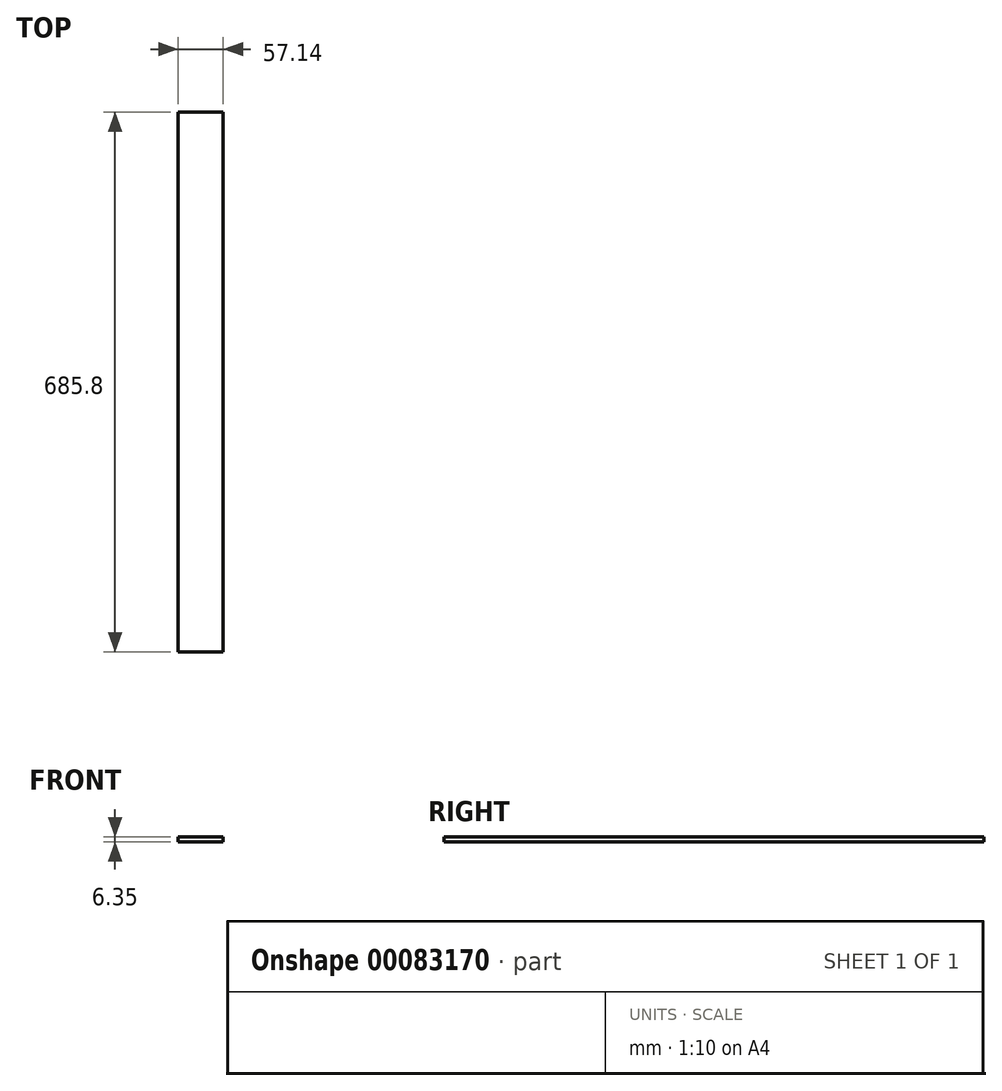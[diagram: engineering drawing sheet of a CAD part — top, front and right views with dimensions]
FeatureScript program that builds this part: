
annotation { "Feature Type Name" : "Feature", "Feature Type Description" : "" }
export const myFeature = defineFeature(function(context is Context, id is Id, definition is map)
    precondition{}
    {
        {
            var Q0;
            Q0=qCreatedBy(makeId("Top.planeOp"),FACE);
            var sketch = newSketch(context, id + "F0", { "sketchPlane" : qUnion([Q0])});
            skLineSegment(sketch, "E0.bottom", {"start": v(28.57, 342.9) * mm, "end": v(-28.57, 342.9) * mm});
            skLineSegment(sketch, "E0.top", {"start": v(28.57, -342.9) * mm, "end": v(-28.57, -342.9) * mm});
            skLineSegment(sketch, "E0.left", {"start": v(28.57, 342.9) * mm, "end": v(28.57, -342.9) * mm});
            skLineSegment(sketch, "E0.right", {"start": v(-28.57, 342.9) * mm, "end": v(-28.57, -342.9) * mm});
            skPoint(sketch, "E0.middle", {"position": v(0, 0) * mm});
            skSolve(sketch);
        }
        {
            var Q0;
            Q0=makeQuery(id+"F0.imprint","IMPRINT",FACE,{"disambiguationData":[TD([[makeQuery(id+"F0.imprint","IMPRINT",EDGE,{"derivedFrom":sQuery(id+"F0.wireOp",EDGE,"E0.bottom")}),1.0]])]});
            extrude(context, id + "F1", {"entities" : qUnion([Q0]), "depth" : 6.35 * mm});
        }
    });
